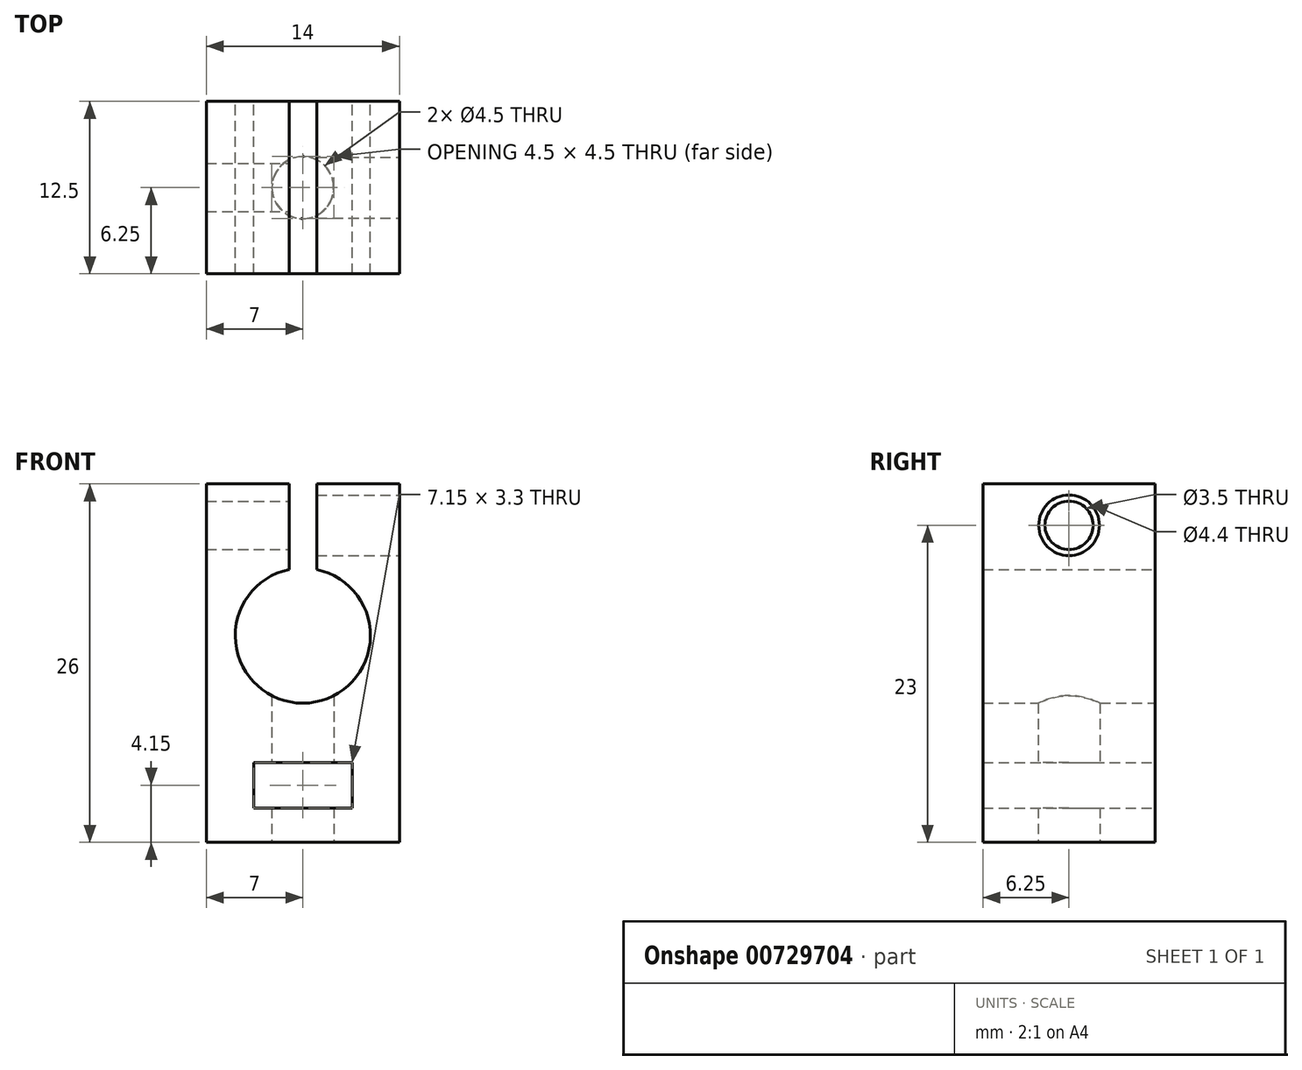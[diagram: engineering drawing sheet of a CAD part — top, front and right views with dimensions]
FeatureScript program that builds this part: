
annotation { "Feature Type Name" : "Feature", "Feature Type Description" : "" }
export const myFeature = defineFeature(function(context is Context, id is Id, definition is map)
    precondition{}
    {
        {
            var Q0;
            Q0=qCreatedBy(makeId("Front.planeOp"),FACE);
            var sketch = newSketch(context, id + "F0", { "sketchPlane" : qUnion([Q0])});
            skCircle(sketch, "E0", {"center": v(0, 0) * mm, "radius": 4.9 * mm});
            skLineSegment(sketch, "E1.bottom", {"start": v(-7, 11) * mm, "end": v(7, 11) * mm});
            skLineSegment(sketch, "E1.top", {"start": v(-7, -15) * mm, "end": v(7, -15) * mm});
            skLineSegment(sketch, "E1.left", {"start": v(-7, 11) * mm, "end": v(-7, -15) * mm});
            skLineSegment(sketch, "E1.right", {"start": v(7, 11) * mm, "end": v(7, -15) * mm});
            skLineSegment(sketch, "E2.bottom", {"start": v(-3.57, -9.2) * mm, "end": v(3.57, -9.2) * mm});
            skLineSegment(sketch, "E2.top", {"start": v(-3.57, -12.5) * mm, "end": v(3.57, -12.5) * mm});
            skLineSegment(sketch, "E2.left", {"start": v(-3.58, -9.2) * mm, "end": v(-3.58, -12.5) * mm});
            skLineSegment(sketch, "E2.right", {"start": v(3.57, -9.2) * mm, "end": v(3.57, -12.5) * mm});
            skSolve(sketch);
        }
        {
            var Q0;
            Q0 = qSketchRegion(id + "F0", true);
            extrude(context, id + "F1", {"entities" : qUnion([Q0]), "depth" : 12.5 * mm, "offsetDistance" : 25 * mm});
        }
        {
            var Q0;
            Q0=makeQuery(id+"F1.opExtrude","SWEPT_FACE",FACE,{"disambiguationData":[OSD([sQuery(id+"F0.wireOp",EDGE,"E1.top")])]});
            var sketch = newSketch(context, id + "F2", { "sketchPlane" : qUnion([Q0])});
            skCircle(sketch, "E3", {"center": v(0, 6.25) * mm, "radius": 2.25 * mm});
            skPoint(sketch, "E3.centerSnap0", {"position": v(-7, 6.25) * mm});
            skSolve(sketch);
        }
        {
            var Q0;
            Q0 = qSketchRegion(id + "F2", true);
            extrude(context, id + "F3", {"entities" : qUnion([Q0]), "operationType" : NewBodyOperationType.REMOVE, "oppositeDirection" : true, "depth" : 15 * mm, "offsetDistance" : 25 * mm});
        }
        {
            var Q0;
            Q0=makeQuery(id+"F1.opExtrude","CAP_FACE",FACE,{"disambiguationData":[OSD([sQuery(id+"F0.wireOp",EDGE,"E0"),sQuery(id+"F0.wireOp",EDGE,"E1.bottom"),sQuery(id+"F0.wireOp",EDGE,"E1.top"),sQuery(id+"F0.wireOp",EDGE,"E1.left"),sQuery(id+"F0.wireOp",EDGE,"E1.right"),sQuery(id+"F0.wireOp",EDGE,"E2.bottom"),sQuery(id+"F0.wireOp",EDGE,"E2.top"),sQuery(id+"F0.wireOp",EDGE,"E2.left"),sQuery(id+"F0.wireOp",EDGE,"E2.right")])],"isStart":false});
            var sketch = newSketch(context, id + "F4", { "sketchPlane" : qUnion([Q0])});
            skLineSegment(sketch, "E4.bottom", {"start": v(-1, 11) * mm, "end": v(1, 11) * mm});
            skLineSegment(sketch, "E4.top", {"start": v(-1, 1.63) * mm, "end": v(1, 1.63) * mm});
            skLineSegment(sketch, "E4.left", {"start": v(-1, 11) * mm, "end": v(-1, 1.63) * mm});
            skLineSegment(sketch, "E4.right", {"start": v(1, 11) * mm, "end": v(1, 1.63) * mm});
            skSolve(sketch);
        }
        {
            var Q0;
            Q0 = qSketchRegion(id + "F4", true);
            extrude(context, id + "F5", {"entities" : qUnion([Q0]), "operationType" : NewBodyOperationType.REMOVE, "endBound" : BoundingType.THROUGH_ALL, "oppositeDirection" : true, "depth" : 25 * mm, "offsetDistance" : 25 * mm});
        }
        {
            var Q0;
            Q0=makeQuery(id+"F1.opExtrude","SWEPT_FACE",FACE,{"disambiguationData":[OSD([sQuery(id+"F0.wireOp",EDGE,"E1.right")])]});
            var sketch = newSketch(context, id + "F6", { "sketchPlane" : qUnion([Q0])});
            skCircle(sketch, "E5", {"center": v(-6.25, 8) * mm, "radius": 1.75 * mm});
            skPoint(sketch, "E5.centerSnap0", {"position": v(-6.25, 11) * mm});
            skSolve(sketch);
        }
        {
            var Q0;
            Q0 = qSketchRegion(id + "F6", true);
            extrude(context, id + "F7", {"entities" : qUnion([Q0]), "operationType" : NewBodyOperationType.REMOVE, "endBound" : BoundingType.THROUGH_ALL, "oppositeDirection" : true, "depth" : 25 * mm, "offsetDistance" : 25 * mm});
        }
        {
            var Q0;
            Q0=makeQuery(id+"F1.opExtrude","SWEPT_FACE",FACE,{"disambiguationData":[OSD([sQuery(id+"F0.wireOp",EDGE,"E1.right")])]});
            var sketch = newSketch(context, id + "F8", { "sketchPlane" : qUnion([Q0])});
            skCircle(sketch, "E6", {"center": v(-6.25, 8) * mm, "radius": 2.2 * mm});
            skSolve(sketch);
        }
        {
            var Q0;
            Q0 = qSketchRegion(id + "F8", true);
            extrude(context, id + "F9", {"entities" : qUnion([Q0]), "operationType" : NewBodyOperationType.REMOVE, "oppositeDirection" : true, "depth" : 6 * mm, "offsetDistance" : 25 * mm});
        }
    });
